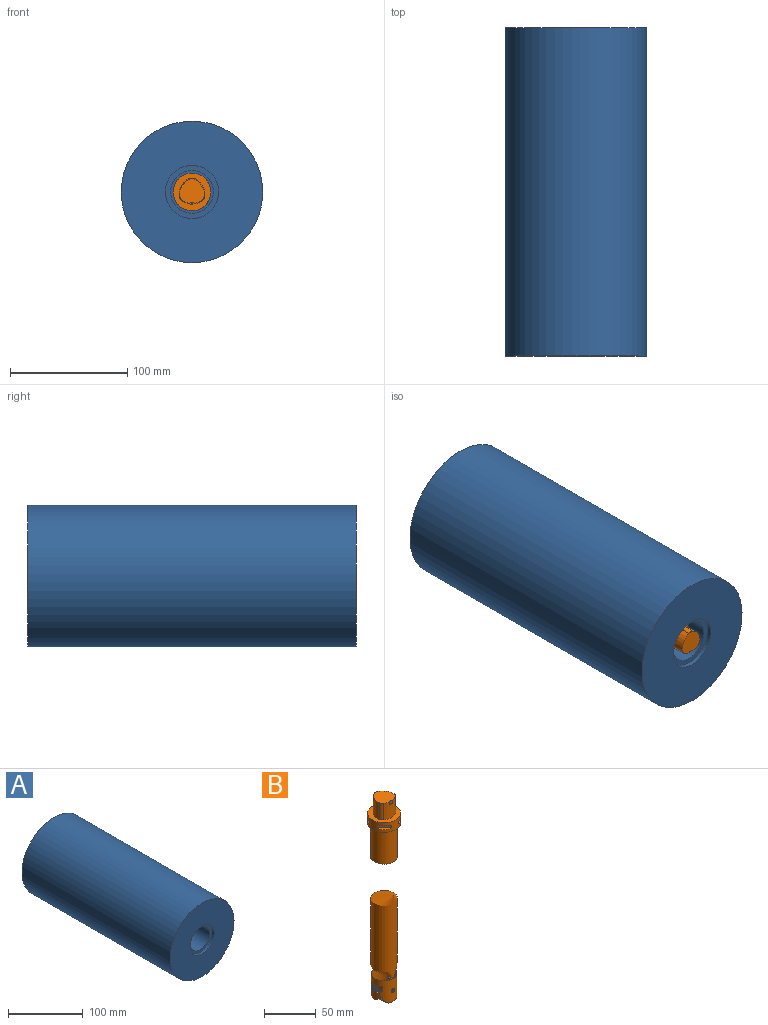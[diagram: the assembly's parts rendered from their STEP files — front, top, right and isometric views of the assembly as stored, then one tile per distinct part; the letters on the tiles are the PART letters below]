
ASSEMBLY  parts=2 mates=1
PART A: 10 faces, bbox 120.5x279.4x120.5 mm
  f0: cylinder r=15.12mm len=200.53mm, axis (0,-1,0), area 19044.7mm2, adj f5,f8
  f1: cylinder r=18.25mm len=36.5mm, axis (0,-1,0), area 3413.5mm2, adj f5,f6
  f2: cylinder r=60.23mm len=279.4mm, axis (0,1,0), area 105740.1mm2, adj f3,f4
  f3: plane 120.47x120.47mm, normal (0,-1,0), area 9788.6mm2, adj f2,f7
  f4: plane 120.47x120.47mm, normal (0,1,0), area 10593.2mm2, adj f2,f9
  f5: plane 36.5x36.5mm, normal (0,-1,0), area 328.6mm2, adj f0,f1
  f6: plane 45.26x45.26mm, normal (0,-1,0), area 562.7mm2, adj f1,f7
  f7: cylinder r=22.63mm len=45.26mm, axis (0,-1,0), area 552.6mm2, adj f3,f6
  f8: plane 32x32mm, normal (0,1,0), area 86.7mm2, adj f0,f9
  f9: cylinder r=16mm len=45.21mm, axis (0,1,0), area 4545.8mm2, adj f4,f8
PART B: 334 faces, bbox 34.1x34.1x237.6 mm
  f0: cylinder r=5mm len=10mm, axis (1,0,0), area 79.2mm2, adj f1,f328,f329,f330,f331,f332,f333
  f1: plane 1.54x0.67mm, normal (0,-1,0), area 0.5mm2, adj f0,f2,f328,f333
  f2: plane 20.16x3.06mm, normal (-0.85,0,-0.53), area 55.5mm2, adj f1,f3,f233,f326,f327,f328,f331,f332
  f3: cone r=11.7mm half-angle=45deg, axis (0,0,1), area 23.6mm2, adj f2,f4,f233,f327
  f4: plane 15.11x12.24mm, normal (1,0,0), area 71.8mm2, adj f3,f5,f7,f9,f10,f11,f13,f14
  f5: plane 1.6x0.58mm, normal (0,0,-1), area 0.1mm2, adj f4,f6,f204,f230
  f6: plane 0.08x0.05mm, normal (-0.34,0.94,0), area 0mm2, adj f5,f204,f229,f230
  f7: plane 0.99x0.36mm, normal (0,-0.13,0.99), area 0mm2, adj f4,f8,f9,f204
  f8: plane 0.08x0.05mm, normal (-0.34,0.93,0.12), area 0mm2, adj f7,f9,f10,f204
  f9: plane 0.86x0.31mm, normal (0.94,0.34,0.04), area 0.1mm2, adj f4,f7,f8,f10
  f10: plane 0.99x0.36mm, normal (0,0.13,-0.99), area 0mm2, adj f4,f8,f9,f204
  f11: plane 0.97x0.36mm, normal (0,-0.25,0.97), area 0mm2, adj f4,f12,f13,f204
  f12: plane 0.08x0.05mm, normal (-0.34,0.91,0.23), area 0mm2, adj f11,f13,f14,f204
  f13: plane 0.85x0.31mm, normal (0.94,0.33,0.09), area 0.1mm2, adj f4,f11,f12,f14
  f14: plane 0.97x0.36mm, normal (0,0.25,-0.97), area 0mm2, adj f4,f12,f13,f204
  f15: plane 0.93x0.37mm, normal (0,-0.37,0.93), area 0mm2, adj f4,f16,f17,f204
  f16: plane 0.08x0.05mm, normal (-0.34,0.87,0.35), area 0mm2, adj f15,f17,f18,f204
  f17: plane 0.82x0.38mm, normal (0.94,0.32,0.13), area 0.1mm2, adj f4,f15,f16,f18
  f18: plane 0.93x0.37mm, normal (0,0.37,-0.93), area 0mm2, adj f4,f16,f17,f204
  f19: plane 0.88x0.48mm, normal (0,-0.48,0.88), area 0mm2, adj f4,f20,f21,f204
  f20: plane 0.07x0.05mm, normal (-0.34,0.82,0.45), area 0mm2, adj f19,f21,f22,f204
  f21: plane 0.78x0.48mm, normal (0.94,0.3,0.16), area 0.1mm2, adj f4,f19,f20,f22
  f22: plane 0.88x0.48mm, normal (0,0.48,-0.88), area 0mm2, adj f4,f20,f21,f204
  f23: plane 1.3x0.94mm, normal (0,-0.59,0.81), area 0.1mm2, adj f4,f24,f25,f204
  f24: plane 0.07x0.06mm, normal (-0.34,0.76,0.55), area 0mm2, adj f23,f25,f26,f204
  f25: plane 1.22x0.92mm, normal (0.94,0.28,0.2), area 0.1mm2, adj f4,f23,f24,f26
  f26: plane 1.3x0.94mm, normal (0,0.59,-0.81), area 0.1mm2, adj f4,f24,f25,f204
  f27: plane 0.73x0.69mm, normal (0,-0.68,0.73), area 0mm2, adj f4,f28,f29,f204
  f28: plane 0.07x0.06mm, normal (-0.34,0.68,0.64), area 0mm2, adj f27,f29,f30,f204
  f29: plane 0.67x0.64mm, normal (0.94,0.25,0.23), area 0.1mm2, adj f4,f27,f28,f30
  f30: plane 0.73x0.69mm, normal (0,0.68,-0.73), area 0mm2, adj f4,f28,f29,f204
  f31: plane 0.77x0.64mm, normal (0,-0.77,0.64), area 0mm2, adj f4,f32,f33,f204
  f32: plane 0.07x0.06mm, normal (-0.34,0.6,0.72), area 0mm2, adj f31,f33,f34,f204
  f33: plane 0.71x0.6mm, normal (0.94,0.22,0.26), area 0.1mm2, adj f4,f31,f32,f34
  f34: plane 0.77x0.64mm, normal (0,0.77,-0.64), area 0mm2, adj f4,f32,f33,f204
  f35: plane 0.84x0.54mm, normal (0,-0.84,0.54), area 0mm2, adj f4,f36,f37,f204
  f36: plane 0.07x0.05mm, normal (-0.34,0.5,0.79), area 0mm2, adj f35,f37,f38,f204
  f37: plane 0.76x0.52mm, normal (0.94,0.18,0.29), area 0.1mm2, adj f4,f35,f36,f38
  f38: plane 0.84x0.54mm, normal (0,0.84,-0.54), area 0mm2, adj f4,f36,f37,f204
  f39: plane 0.91x0.43mm, normal (0,-0.9,0.43), area 0mm2, adj f4,f40,f41,f204
  f40: plane 0.08x0.05mm, normal (-0.34,0.4,0.85), area 0mm2, adj f39,f41,f42,f204
  f41: plane 0.8x0.43mm, normal (0.94,0.15,0.31), area 0.1mm2, adj f4,f39,f40,f42
  f42: plane 0.91x0.43mm, normal (0,0.9,-0.43), area 0mm2, adj f4,f40,f41,f204
  f43: plane 1.52x0.58mm, normal (0,-0.95,0.31), area 0.1mm2, adj f4,f44,f45,f204
  f44: plane 0.08x0.05mm, normal (-0.34,0.29,0.89), area 0mm2, adj f43,f45,f46,f204
  f45: plane 1.41x0.53mm, normal (0.94,0.11,0.33), area 0.1mm2, adj f4,f43,f44,f46
  f46: plane 1.52x0.58mm, normal (0,0.95,-0.31), area 0.1mm2, adj f4,f44,f45,f204
  f47: plane 0.98x0.36mm, normal (0,-0.98,0.19), area 0mm2, adj f4,f48,f49,f204
  f48: plane 0.08x0.05mm, normal (-0.34,0.18,0.92), area 0mm2, adj f47,f49,f50,f204
  f49: plane 0.85x0.31mm, normal (0.94,0.06,0.34), area 0.1mm2, adj f4,f47,f48,f50
  f50: plane 0.98x0.36mm, normal (0,0.98,-0.19), area 0mm2, adj f4,f48,f49,f204
  f51: plane 1x0.36mm, normal (0,-1,0.06), area 0mm2, adj f4,f52,f53,f204
  f52: plane 0.08x0.05mm, normal (-0.34,0.06,0.94), area 0mm2, adj f51,f53,f54,f204
  f53: plane 0.86x0.31mm, normal (0.94,0.02,0.34), area 0.1mm2, adj f4,f51,f52,f54
  f54: plane 1x0.36mm, normal (0,1,-0.06), area 0mm2, adj f4,f52,f53,f204
  f55: plane 1x0.36mm, normal (0,-1,-0.06), area 0mm2, adj f4,f56,f57,f204
  f56: plane 0.08x0.05mm, normal (-0.34,-0.06,0.94), area 0mm2, adj f55,f57,f58,f204
  f57: plane 0.86x0.31mm, normal (0.94,-0.02,0.34), area 0.1mm2, adj f4,f55,f56,f58
  f58: plane 1x0.36mm, normal (0,1,0.06), area 0mm2, adj f4,f56,f57,f204
  f59: plane 0.98x0.36mm, normal (0,-0.98,-0.19), area 0mm2, adj f4,f60,f61,f204
  f60: plane 0.08x0.05mm, normal (-0.34,-0.18,0.92), area 0mm2, adj f59,f61,f62,f204
  f61: plane 0.85x0.31mm, normal (0.94,-0.06,0.34), area 0.1mm2, adj f4,f59,f60,f62
  f62: plane 0.98x0.36mm, normal (0,0.98,0.19), area 0mm2, adj f4,f60,f61,f204
  f63: plane 1.52x0.58mm, normal (0,-0.95,-0.31), area 0.1mm2, adj f4,f64,f65,f204
  f64: plane 0.08x0.05mm, normal (-0.34,-0.29,0.89), area 0mm2, adj f63,f65,f66,f204
  f65: plane 1.41x0.53mm, normal (0.94,-0.11,0.33), area 0.1mm2, adj f4,f63,f64,f66
  f66: plane 1.52x0.58mm, normal (0,0.95,0.31), area 0.1mm2, adj f4,f64,f65,f204
  f67: plane 0.91x0.43mm, normal (0,-0.9,-0.43), area 0mm2, adj f4,f68,f69,f204
  f68: plane 0.08x0.05mm, normal (-0.34,-0.4,0.85), area 0mm2, adj f67,f69,f70,f204
  f69: plane 0.8x0.43mm, normal (0.94,-0.15,0.31), area 0.1mm2, adj f4,f67,f68,f70
  f70: plane 0.91x0.43mm, normal (0,0.9,0.43), area 0mm2, adj f4,f68,f69,f204
  f71: plane 0.84x0.54mm, normal (0,-0.84,-0.54), area 0mm2, adj f4,f72,f73,f204
  f72: plane 0.07x0.05mm, normal (-0.34,-0.5,0.79), area 0mm2, adj f71,f73,f74,f204
  f73: plane 0.76x0.52mm, normal (0.94,-0.18,0.29), area 0.1mm2, adj f4,f71,f72,f74
  f74: plane 0.84x0.54mm, normal (0,0.84,0.54), area 0mm2, adj f4,f72,f73,f204
  f75: plane 0.77x0.64mm, normal (0,-0.77,-0.64), area 0mm2, adj f4,f76,f77,f204
  f76: plane 0.07x0.06mm, normal (-0.34,-0.6,0.72), area 0mm2, adj f75,f77,f78,f204
  f77: plane 0.71x0.6mm, normal (0.94,-0.22,0.26), area 0.1mm2, adj f4,f75,f76,f78
  f78: plane 0.77x0.64mm, normal (0,0.77,0.64), area 0mm2, adj f4,f76,f77,f204
  f79: plane 0.73x0.69mm, normal (0,-0.68,-0.73), area 0mm2, adj f4,f80,f81,f204
  f80: plane 0.07x0.06mm, normal (-0.34,-0.68,0.64), area 0mm2, adj f79,f81,f82,f204
  f81: plane 0.67x0.64mm, normal (0.94,-0.25,0.23), area 0.1mm2, adj f4,f79,f80,f82
  f82: plane 0.73x0.69mm, normal (0,0.68,0.73), area 0mm2, adj f4,f80,f81,f204
  f83: plane 1.3x0.94mm, normal (0,-0.59,-0.81), area 0.1mm2, adj f4,f84,f85,f204
  f84: plane 0.07x0.06mm, normal (-0.34,-0.76,0.55), area 0mm2, adj f83,f85,f86,f204
  f85: plane 1.22x0.92mm, normal (0.94,-0.28,0.2), area 0.1mm2, adj f4,f83,f84,f86
  f86: plane 1.3x0.94mm, normal (0,0.59,0.81), area 0.1mm2, adj f4,f84,f85,f204
  f87: plane 0.88x0.48mm, normal (0,-0.48,-0.88), area 0mm2, adj f4,f88,f89,f204
  f88: plane 0.07x0.05mm, normal (-0.34,-0.82,0.45), area 0mm2, adj f87,f89,f90,f204
  f89: plane 0.78x0.48mm, normal (0.94,-0.3,0.16), area 0.1mm2, adj f4,f87,f88,f90
  f90: plane 0.88x0.48mm, normal (0,0.48,0.88), area 0mm2, adj f4,f88,f89,f204
  f91: plane 0.93x0.37mm, normal (0,-0.37,-0.93), area 0mm2, adj f4,f92,f93,f204
  f92: plane 0.08x0.05mm, normal (-0.34,-0.87,0.35), area 0mm2, adj f91,f93,f94,f204
  f93: plane 0.82x0.38mm, normal (0.94,-0.32,0.13), area 0.1mm2, adj f4,f91,f92,f94
  f94: plane 0.93x0.37mm, normal (0,0.37,0.93), area 0mm2, adj f4,f92,f93,f204
  f95: plane 0.97x0.36mm, normal (0,-0.25,-0.97), area 0mm2, adj f4,f96,f97,f204
  f96: plane 0.08x0.05mm, normal (-0.34,-0.91,0.23), area 0mm2, adj f95,f97,f98,f204
  f97: plane 0.85x0.31mm, normal (0.94,-0.33,0.09), area 0.1mm2, adj f4,f95,f96,f98
  f98: plane 0.97x0.36mm, normal (0,0.25,0.97), area 0mm2, adj f4,f96,f97,f204
  f99: plane 0.99x0.36mm, normal (0,-0.13,-0.99), area 0mm2, adj f4,f100,f101,f204
  f100: plane 0.08x0.05mm, normal (-0.34,-0.93,0.12), area 0mm2, adj f99,f101,f102,f204
  f101: plane 0.86x0.31mm, normal (0.94,-0.34,0.04), area 0.1mm2, adj f4,f99,f100,f102
  f102: plane 0.99x0.36mm, normal (0,0.13,0.99), area 0mm2, adj f4,f100,f101,f204
  f103: plane 1.6x0.58mm, normal (0,0,-1), area 0.1mm2, adj f4,f104,f105,f204
  f104: plane 0.08x0.05mm, normal (-0.34,-0.94,0), area 0mm2, adj f103,f105,f106,f204
  f105: plane 1.45x0.53mm, normal (0.94,-0.34,0), area 0.1mm2, adj f4,f103,f104,f106
  f106: plane 1.6x0.58mm, normal (0,0,1), area 0.1mm2, adj f4,f104,f105,f204
  f107: plane 0.99x0.36mm, normal (0,0.13,-0.99), area 0mm2, adj f4,f108,f109,f204
  f108: plane 0.08x0.05mm, normal (-0.34,-0.93,-0.12), area 0mm2, adj f107,f109,f110,f204
  f109: plane 0.86x0.31mm, normal (0.94,-0.34,-0.04), area 0.1mm2, adj f4,f107,f108,f110
  f110: plane 0.99x0.36mm, normal (0,-0.13,0.99), area 0mm2, adj f4,f108,f109,f204
  f111: plane 0.97x0.36mm, normal (0,0.25,-0.97), area 0mm2, adj f4,f112,f113,f204
  f112: plane 0.08x0.05mm, normal (-0.34,-0.91,-0.23), area 0mm2, adj f111,f113,f114,f204
  f113: plane 0.85x0.31mm, normal (0.94,-0.33,-0.09), area 0.1mm2, adj f4,f111,f112,f114
  f114: plane 0.97x0.36mm, normal (0,-0.25,0.97), area 0mm2, adj f4,f112,f113,f204
  f115: plane 0.93x0.37mm, normal (0,0.37,-0.93), area 0mm2, adj f4,f116,f117,f204
  f116: plane 0.08x0.05mm, normal (-0.34,-0.87,-0.35), area 0mm2, adj f115,f117,f118,f204
  f117: plane 0.82x0.38mm, normal (0.94,-0.32,-0.13), area 0.1mm2, adj f4,f115,f116,f118
  f118: plane 0.93x0.37mm, normal (0,-0.37,0.93), area 0mm2, adj f4,f116,f117,f204
  f119: plane 0.88x0.48mm, normal (0,0.48,-0.88), area 0mm2, adj f4,f120,f121,f204
  f120: plane 0.07x0.05mm, normal (-0.34,-0.82,-0.45), area 0mm2, adj f119,f121,f122,f204
  f121: plane 0.78x0.48mm, normal (0.94,-0.3,-0.16), area 0.1mm2, adj f4,f119,f120,f122
  f122: plane 0.88x0.48mm, normal (0,-0.48,0.88), area 0mm2, adj f4,f120,f121,f204
  f123: plane 1.3x0.94mm, normal (0,0.59,-0.81), area 0.1mm2, adj f4,f124,f125,f204
  f124: plane 0.07x0.06mm, normal (-0.34,-0.76,-0.55), area 0mm2, adj f123,f125,f126,f204
  f125: plane 1.22x0.92mm, normal (0.94,-0.28,-0.2), area 0.1mm2, adj f4,f123,f124,f126
  f126: plane 1.3x0.94mm, normal (0,-0.59,0.81), area 0.1mm2, adj f4,f124,f125,f204
  f127: plane 0.73x0.69mm, normal (0,0.68,-0.73), area 0mm2, adj f4,f128,f129,f204
  f128: plane 0.07x0.06mm, normal (-0.34,-0.68,-0.64), area 0mm2, adj f127,f129,f130,f204
  f129: plane 0.67x0.64mm, normal (0.94,-0.25,-0.23), area 0.1mm2, adj f4,f127,f128,f130
  f130: plane 0.73x0.69mm, normal (0,-0.68,0.73), area 0mm2, adj f4,f128,f129,f204
  f131: plane 0.77x0.64mm, normal (0,0.77,-0.64), area 0mm2, adj f4,f132,f133,f204
  f132: plane 0.07x0.06mm, normal (-0.34,-0.6,-0.72), area 0mm2, adj f131,f133,f134,f204
  f133: plane 0.71x0.6mm, normal (0.94,-0.22,-0.26), area 0.1mm2, adj f4,f131,f132,f134
  f134: plane 0.77x0.64mm, normal (0,-0.77,0.64), area 0mm2, adj f4,f132,f133,f204
  f135: plane 0.84x0.54mm, normal (0,0.84,-0.54), area 0mm2, adj f4,f136,f137,f204
  f136: plane 0.07x0.05mm, normal (-0.34,-0.5,-0.79), area 0mm2, adj f135,f137,f138,f204
  f137: plane 0.76x0.52mm, normal (0.94,-0.18,-0.29), area 0.1mm2, adj f4,f135,f136,f138
  f138: plane 0.84x0.54mm, normal (0,-0.84,0.54), area 0mm2, adj f4,f136,f137,f204
  f139: plane 0.91x0.43mm, normal (0,0.9,-0.43), area 0mm2, adj f4,f140,f141,f204
  f140: plane 0.08x0.05mm, normal (-0.34,-0.4,-0.85), area 0mm2, adj f139,f141,f142,f204
  f141: plane 0.8x0.43mm, normal (0.94,-0.15,-0.31), area 0.1mm2, adj f4,f139,f140,f142
  f142: plane 0.91x0.43mm, normal (0,-0.9,0.43), area 0mm2, adj f4,f140,f141,f204
  f143: plane 1.52x0.58mm, normal (0,0.95,-0.31), area 0.1mm2, adj f4,f144,f145,f204
  f144: plane 0.08x0.05mm, normal (-0.34,-0.29,-0.89), area 0mm2, adj f143,f145,f146,f204
  f145: plane 1.41x0.53mm, normal (0.94,-0.11,-0.33), area 0.1mm2, adj f4,f143,f144,f146
  f146: plane 1.52x0.58mm, normal (0,-0.95,0.31), area 0.1mm2, adj f4,f144,f145,f204
  f147: plane 0.98x0.36mm, normal (0,0.98,-0.19), area 0mm2, adj f4,f148,f149,f204
  f148: plane 0.08x0.05mm, normal (-0.34,-0.18,-0.92), area 0mm2, adj f147,f149,f150,f204
  f149: plane 0.85x0.31mm, normal (0.94,-0.06,-0.34), area 0.1mm2, adj f4,f147,f148,f150
  f150: plane 0.98x0.36mm, normal (0,-0.98,0.19), area 0mm2, adj f4,f148,f149,f204
  f151: plane 1x0.36mm, normal (0,1,-0.06), area 0mm2, adj f4,f152,f153,f204
  f152: plane 0.08x0.05mm, normal (-0.34,-0.06,-0.94), area 0mm2, adj f151,f153,f154,f204
  f153: plane 0.86x0.31mm, normal (0.94,-0.02,-0.34), area 0.1mm2, adj f4,f151,f152,f154
  f154: plane 1x0.36mm, normal (0,-1,0.06), area 0mm2, adj f4,f152,f153,f204
  f155: cone r=2.25mm half-angle=70deg, axis (-1,0,0), area 0mm2, adj f4,f156,f204
  f156: plane 1x0.36mm, normal (0,1,0.06), area 0mm2, adj f4,f155,f157,f158
  f157: plane 0.08x0.05mm, normal (-0.34,0.06,-0.94), area 0mm2, adj f156,f158,f159,f204
  f158: plane 0.86x0.31mm, normal (0.94,0.02,-0.34), area 0.1mm2, adj f4,f156,f157,f159
  f159: plane 1x0.36mm, normal (0,-1,-0.06), area 0mm2, adj f4,f157,f158,f204
  f160: plane 0.98x0.36mm, normal (0,0.98,0.19), area 0mm2, adj f4,f161,f162,f204
  f161: plane 0.08x0.05mm, normal (-0.34,0.18,-0.92), area 0mm2, adj f160,f162,f163,f204
  f162: plane 0.85x0.31mm, normal (0.94,0.06,-0.34), area 0.1mm2, adj f4,f160,f161,f163
  f163: plane 0.98x0.36mm, normal (0,-0.98,-0.19), area 0mm2, adj f4,f161,f162,f204
  f164: plane 1.52x0.58mm, normal (0,0.95,0.31), area 0.1mm2, adj f4,f165,f166,f204
  f165: plane 0.08x0.05mm, normal (-0.34,0.29,-0.89), area 0mm2, adj f164,f166,f167,f204
  f166: plane 1.41x0.53mm, normal (0.94,0.11,-0.33), area 0.1mm2, adj f4,f164,f165,f167
  f167: plane 1.52x0.58mm, normal (0,-0.95,-0.31), area 0.1mm2, adj f4,f165,f166,f204
  f168: plane 0.91x0.43mm, normal (0,0.9,0.43), area 0mm2, adj f4,f169,f170,f204
  f169: plane 0.08x0.05mm, normal (-0.34,0.4,-0.85), area 0mm2, adj f168,f170,f171,f204
  f170: plane 0.8x0.43mm, normal (0.94,0.15,-0.31), area 0.1mm2, adj f4,f168,f169,f171
  f171: plane 0.91x0.43mm, normal (0,-0.9,-0.43), area 0mm2, adj f4,f169,f170,f204
  f172: plane 0.84x0.54mm, normal (0,0.84,0.54), area 0mm2, adj f4,f173,f174,f204
  f173: plane 0.07x0.05mm, normal (-0.34,0.5,-0.79), area 0mm2, adj f172,f174,f175,f204
  f174: plane 0.76x0.52mm, normal (0.94,0.18,-0.29), area 0.1mm2, adj f4,f172,f173,f175
  f175: plane 0.84x0.54mm, normal (0,-0.84,-0.54), area 0mm2, adj f4,f173,f174,f204
  f176: plane 0.77x0.64mm, normal (0,0.77,0.64), area 0mm2, adj f4,f177,f178,f204
  f177: plane 0.07x0.06mm, normal (-0.34,0.6,-0.72), area 0mm2, adj f176,f178,f179,f204
  f178: plane 0.71x0.6mm, normal (0.94,0.22,-0.26), area 0.1mm2, adj f4,f176,f177,f179
  f179: plane 0.77x0.64mm, normal (0,-0.77,-0.64), area 0mm2, adj f4,f177,f178,f204
  f180: plane 0.73x0.69mm, normal (0,0.68,0.73), area 0mm2, adj f4,f181,f182,f204
  f181: plane 0.07x0.06mm, normal (-0.34,0.68,-0.64), area 0mm2, adj f180,f182,f183,f204
  f182: plane 0.67x0.64mm, normal (0.94,0.25,-0.23), area 0.1mm2, adj f4,f180,f181,f183
  f183: plane 0.73x0.69mm, normal (0,-0.68,-0.73), area 0mm2, adj f4,f181,f182,f204
  f184: plane 1.3x0.94mm, normal (0,0.59,0.81), area 0.1mm2, adj f4,f185,f186,f204
  f185: plane 0.07x0.06mm, normal (-0.34,0.76,-0.55), area 0mm2, adj f184,f186,f187,f204
  f186: plane 1.22x0.92mm, normal (0.94,0.28,-0.2), area 0.1mm2, adj f4,f184,f185,f187
  f187: plane 1.3x0.94mm, normal (0,-0.59,-0.81), area 0.1mm2, adj f4,f185,f186,f204
  f188: plane 0.88x0.48mm, normal (0,0.48,0.88), area 0mm2, adj f4,f189,f190,f204
  f189: plane 0.07x0.05mm, normal (-0.34,0.82,-0.45), area 0mm2, adj f188,f190,f191,f204
  f190: plane 0.78x0.48mm, normal (0.94,0.3,-0.16), area 0.1mm2, adj f4,f188,f189,f191
  f191: plane 0.88x0.48mm, normal (0,-0.48,-0.88), area 0mm2, adj f4,f189,f190,f204
  f192: plane 0.93x0.37mm, normal (0,0.37,0.93), area 0mm2, adj f4,f193,f194,f204
  f193: plane 0.08x0.05mm, normal (-0.34,0.87,-0.35), area 0mm2, adj f192,f194,f195,f204
  f194: plane 0.82x0.38mm, normal (0.94,0.32,-0.13), area 0.1mm2, adj f4,f192,f193,f195
  f195: plane 0.93x0.37mm, normal (0,-0.37,-0.93), area 0mm2, adj f4,f193,f194,f204
  f196: plane 0.97x0.36mm, normal (0,0.25,0.97), area 0mm2, adj f4,f197,f198,f204
  f197: plane 0.08x0.05mm, normal (-0.34,0.91,-0.23), area 0mm2, adj f196,f198,f199,f204
  f198: plane 0.85x0.31mm, normal (0.94,0.33,-0.09), area 0.1mm2, adj f4,f196,f197,f199
  f199: plane 0.97x0.36mm, normal (0,-0.25,-0.97), area 0mm2, adj f4,f197,f198,f204
  f200: plane 0.99x0.36mm, normal (0,0.13,0.99), area 0mm2, adj f4,f201,f202,f204
  f201: plane 0.08x0.05mm, normal (-0.34,0.93,-0.12), area 0mm2, adj f200,f202,f203,f204
  f202: plane 0.86x0.31mm, normal (0.94,0.34,-0.04), area 0.1mm2, adj f4,f200,f201,f203
  f203: plane 0.99x0.36mm, normal (0,-0.13,-0.99), area 0mm2, adj f4,f201,f202,f204
  f204: cone r=2.25mm half-angle=70deg, axis (-1,0,0), area 94.8mm2, adj f4,f5,f6,f7,f8,f10,f11,f12
  f205: plane 4.51x4.51mm, normal (1,0,0), area 8mm2, adj f204,f206
  f206: cone r=1.59mm half-angle=30deg, axis (1,0,0), area 1.7mm2, adj f205,f207
  f207: cylinder r=1.5mm len=3mm, axis (-1,0,0), area 3.3mm2, adj f206,f208
  f208: cone r=1.5mm half-angle=45deg, axis (1,0,0), area 1.9mm2, adj f207,f209,f211,f213,f214,f216,f217,f219
  f209: plane 2.21x0.43mm, normal (0,-0.5,-0.87), area 0.9mm2, adj f208,f210,f226,f228
  f210: plane 0.76x0.22mm, normal (1,0,0), area 0.1mm2, adj f209,f226,f228
  f211: plane 2.21x0.43mm, normal (0,-0.5,-0.87), area 0.9mm2, adj f208,f212,f213,f226
  f212: plane 0.66x0.38mm, normal (1,0,0), area 0.1mm2, adj f211,f213,f226
  f213: plane 2.21x0.49mm, normal (0,-1,0), area 0.9mm2, adj f208,f211,f212,f226
  f214: plane 2.21x0.49mm, normal (0,-1,0), area 0.9mm2, adj f208,f215,f216,f226
  f215: plane 0.66x0.38mm, normal (1,0,0), area 0.1mm2, adj f214,f216,f226
  f216: plane 2.21x0.43mm, normal (0,-0.5,0.87), area 0.9mm2, adj f208,f214,f215,f226
  f217: plane 2.21x0.43mm, normal (0,-0.5,0.87), area 0.9mm2, adj f208,f218,f219,f226
  f218: plane 0.76x0.22mm, normal (1,0,0), area 0.1mm2, adj f217,f219,f226
  f219: plane 2.21x0.43mm, normal (0,0.5,0.87), area 0.9mm2, adj f208,f217,f218,f226
  f220: plane 2.21x0.43mm, normal (0,0.5,0.87), area 0.9mm2, adj f208,f221,f222,f226
  f221: plane 0.66x0.38mm, normal (1,0,0), area 0.1mm2, adj f220,f222,f226
  f222: plane 2.21x0.49mm, normal (0,1,0), area 0.9mm2, adj f208,f220,f221,f226
  f223: plane 2.21x0.49mm, normal (0,1,0), area 0.9mm2, adj f208,f224,f225,f226
  f224: plane 0.66x0.38mm, normal (1,0,0), area 0.1mm2, adj f223,f225,f226
  f225: plane 2.21x0.43mm, normal (0,0.5,-0.87), area 0.9mm2, adj f208,f223,f224,f226
  f226: cylinder r=1.3mm len=2.6mm, axis (1,0,0), area 12mm2, adj f208,f209,f210,f211,f212,f213,f214,f215
  f227: cone r=1.3mm half-angle=70deg, axis (1,0,0), area 5.7mm2, adj f226
  f228: plane 2.21x0.43mm, normal (0,0.5,-0.87), area 0.9mm2, adj f208,f209,f210,f226
  f229: plane 1.6x0.58mm, normal (0,0,1), area 0.1mm2, adj f4,f6,f204,f230
  f230: plane 1.45x0.53mm, normal (0.94,0.34,0), area 0.1mm2, adj f4,f5,f6,f229
  f231: cone r=11.7mm half-angle=45deg, axis (0,0,1), area 20.6mm2, adj f4,f233,f326,f327
  f232: plane 12.12x1.57mm, normal (0.71,0,-0.71), area 18.1mm2, adj f4,f233
  f233: cylinder r=12.5mm len=26.7mm, axis (0,0,-1), area 1534.3mm2, adj f2,f3,f4,f231,f232,f234,f244,f248
  f234: cylinder r=2.12mm len=4.25mm, axis (0,1,0), area 10.3mm2, adj f233,f235
  f235: plane 4.25x4.25mm, normal (0,-1,0), area 1.6mm2, adj f234,f236
  f236: cylinder r=2mm len=4mm, axis (0,1,0), area 8.2mm2, adj f235,f237
  f237: cone r=2mm half-angle=45deg, axis (0,1,0), area 0.9mm2, adj f236,f238
  f238: plane 3.9x3.9mm, normal (0,-1,0), area 4.9mm2, adj f237,f239
  f239: cone r=1.5mm half-angle=60deg, axis (0,-1,0), area 7.3mm2, adj f238,f240
  f240: cylinder r=0.5mm len=1mm, axis (0,1,0), area 0.3mm2, adj f239,f241
  f241: cone r=0.75mm half-angle=60deg, axis (0,1,0), area 0.1mm2, adj f240,f242
  f242: plane 1.08x1.08mm, normal (0,-1,0), area 0.2mm2, adj f241,f243
  f243: sphere r=0.65mm, area 0.9mm2, adj f242
  f244: cylinder r=2.01mm len=4.02mm, axis (0,-1,0), area 9.7mm2, adj f233,f245
  f245: plane 4.02x4.02mm, normal (0,1,0), area 0.1mm2, adj f244,f246
  f246: cylinder r=2mm len=4mm, axis (0,-1,0), area 4.5mm2, adj f245,f247
  f247: sphere r=5.8mm, area 12.8mm2, adj f246
  f248: cylinder r=2.6mm len=5.19mm, axis (0,-1,0), area 7.2mm2, adj f233,f249
  f249: plane 5.19x5.19mm, normal (0,1,0), area 1.5mm2, adj f248,f250
  f250: cylinder r=2.5mm len=5mm, axis (0,-1,0), area 2.3mm2, adj f249,f251
  f251: cone r=2mm half-angle=45deg, axis (0,-1,0), area 10mm2, adj f250,f252
  f252: plane 4x4mm, normal (0,1,0), area 7.2mm2, adj f251,f253,f262,f263,f264,f265,f266
  f253: plane 3.2x1.22mm, normal (-0.85,0,0.53), area 4.6mm2, adj f252,f254,f261,f262,f266
  f254: plane 1.25x0.38mm, normal (0,1,0), area 0.1mm2, adj f253,f255,f266
  f255: cylinder r=1.25mm len=2.5mm, axis (0,-1,0), area 3.9mm2, adj f254,f256,f257,f258,f259,f260,f261
  f256: plane 1.06x0.67mm, normal (0,1,0), area 0.1mm2, adj f255,f262,f263
  f257: plane 1.25x0.38mm, normal (0,1,0), area 0.1mm2, adj f255,f263,f264
  f258: plane 1.11x0.61mm, normal (0,1,0), area 0.1mm2, adj f255,f264,f265
  f259: plane 1.06x0.67mm, normal (0,1,0), area 0.1mm2, adj f255,f265,f266
  f260: cone r=1.25mm half-angle=70deg, axis (0,1,0), area 5.2mm2, adj f255
  f261: plane 1.11x0.61mm, normal (0,1,0), area 0.1mm2, adj f253,f255,f262
  f262: plane 3.2x1.44mm, normal (0.04,0,1), area 4.6mm2, adj f252,f253,f256,f261,f263
  f263: plane 3.2x1.28mm, normal (0.88,0,0.47), area 4.6mm2, adj f252,f256,f257,f262,f264
  f264: plane 3.2x1.22mm, normal (0.85,0,-0.53), area 4.6mm2, adj f252,f257,f258,f263,f265
  f265: plane 3.2x1.44mm, normal (-0.04,0,-1), area 4.6mm2, adj f252,f258,f259,f264,f266
  f266: plane 3.2x1.28mm, normal (-0.88,0,-0.47), area 4.6mm2, adj f252,f253,f254,f259,f265
  f267: plane 6.1x2.35mm, normal (0,0,1), area 1mm2, adj f233,f268,f299
  f268: torus R=32.4mm, axis (0,0,-1), area 3.6mm2, adj f233,f267,f271,f299
  f269: plane 13.8x2.23mm, normal (0,0,-1), area 12.6mm2, adj f233,f270
  f270: torus R=32.4mm, axis (0,0,1), area 9.3mm2, adj f233,f269,f271
  f271: cylinder r=32mm len=15.48mm, axis (0,0,1), area 51.3mm2, adj f233,f268,f270,f272,f294,f295,f296,f297
  f272: plane 3x1.2mm, normal (0,0,-1), area 3.5mm2, adj f271,f273,f294,f296
  f273: cylinder r=0.4mm len=3mm, axis (0,-1,0), area 1.9mm2, adj f272,f274,f276,f293
  f274: torus R=2.1mm, axis (1,0,0), area 4.6mm2, adj f273,f275,f276,f294
  f275: cylinder r=0.4mm len=3mm, axis (0,-1,0), area 1.9mm2, adj f274,f276,f293,f295
  f276: plane 7.4x4.4mm, normal (-1,0,0), area 23.3mm2, adj f273,f274,f275,f277,f293
  f277: cylinder r=1mm len=2.04mm, axis (1,0.08,0), area 3mm2, adj f276,f278
  f278: cone r=1mm half-angle=30deg, axis (1,0.08,0), area 2.7mm2, adj f277,f279
  f279: plane 1.51x1.5mm, normal (-1,-0.08,0), area 1.1mm2, adj f278,f280,f288,f289,f290,f291,f292
  f280: plane 0.83x0.48mm, normal (0.05,-0.6,-0.8), area 0.4mm2, adj f279,f281,f287,f288,f292
  f281: plane 0.45x0.16mm, normal (-1,-0.08,0), area 0mm2, adj f280,f282,f292
  f282: cone r=1.73mm half-angle=60deg, axis (-1,-0.08,0), area 0.7mm2, adj f281,f283,f284,f285,f286,f287
  f283: plane 0.36x0.27mm, normal (-1,-0.08,0), area 0mm2, adj f282,f288,f289
  f284: plane 0.45x0.16mm, normal (-1,-0.08,0), area 0mm2, adj f282,f289,f290
  f285: plane 0.42x0.21mm, normal (-1,-0.08,0), area 0mm2, adj f282,f290,f291
  f286: plane 0.36x0.27mm, normal (-1,-0.08,0), area 0mm2, adj f282,f291,f292
  f287: plane 0.42x0.21mm, normal (-1,-0.08,0), area 0mm2, adj f280,f282,f288
  f288: plane 0.8x0.52mm, normal (0.08,-0.99,0.13), area 0.4mm2, adj f279,f280,f283,f287,f289
  f289: plane 0.84x0.54mm, normal (0.03,-0.38,0.92), area 0.4mm2, adj f279,f283,f284,f288,f290
  f290: plane 0.83x0.48mm, normal (-0.05,0.6,0.8), area 0.4mm2, adj f279,f284,f285,f289,f291
  f291: plane 0.8x0.52mm, normal (-0.08,0.99,-0.13), area 0.4mm2, adj f279,f285,f286,f290,f292
  f292: plane 0.84x0.54mm, normal (-0.03,0.38,-0.92), area 0.4mm2, adj f279,f280,f281,f286,f291
  f293: torus R=2.1mm, axis (1,0,0), area 4.6mm2, adj f273,f275,f276,f296
  f294: cylinder r=2.5mm len=5mm, axis (-1,0,0), area 9mm2, adj f271,f272,f274,f295
  f295: plane 3x1.2mm, normal (0,0,1), area 3.5mm2, adj f271,f275,f294,f296
  f296: cylinder r=2.5mm len=5mm, axis (-1,0,0), area 9.2mm2, adj f271,f272,f293,f295
  f297: torus R=32.4mm, axis (0,0,-1), area 2.8mm2, adj f233,f271,f298,f299
  f298: plane 3.16x0.46mm, normal (0,0,1), area 0.5mm2, adj f233,f297,f299
  f299: plane 13.37x2.04mm, normal (-0.85,0,0.53), area 5.4mm2, adj f233,f267,f268,f297,f298,f330
  f300: cone r=13mm half-angle=0.2deg, axis (0,0,1), area 11055.3mm2, adj f233,f301
  f301: cylinder r=13mm len=39.5mm, axis (0,0,-1), area 3226.4mm2, adj f300,f302
  f302: plane 32x32mm, normal (0,0,-1), area 273.3mm2, adj f301,f303
  f303: cylinder r=16mm len=32mm, axis (0,0,-1), area 1001.3mm2, adj f302,f304,f305,f306,f307,f308,f309,f310
  f304: plane 12.64x12.64mm, normal (0.35,0.35,0.87), area 21.3mm2, adj f303,f306
  f305: plane 12.64x12.64mm, normal (0.35,0.35,-0.87), area 21.3mm2, adj f303,f306
  f306: plane 10.52x10.52mm, normal (0.71,0.71,0), area 37.2mm2, adj f303,f304,f305
  f307: plane 12.64x12.64mm, normal (-0.35,-0.35,0.87), area 21.3mm2, adj f303,f309
  f308: plane 12.64x12.64mm, normal (-0.35,-0.35,-0.87), area 21.3mm2, adj f303,f309
  f309: plane 10.52x10.52mm, normal (-0.71,-0.71,0), area 37.2mm2, adj f303,f307,f308
  f310: plane 12.64x12.64mm, normal (-0.35,0.35,0.87), area 21.3mm2, adj f303,f312
  f311: plane 12.64x12.64mm, normal (-0.35,0.35,-0.87), area 21.3mm2, adj f303,f312
  f312: plane 10.52x10.52mm, normal (-0.71,0.71,0), area 37.2mm2, adj f303,f310,f311
  f313: plane 12.64x12.64mm, normal (0.35,-0.35,0.87), area 21.3mm2, adj f303,f315
  f314: plane 12.64x12.64mm, normal (0.35,-0.35,-0.87), area 21.3mm2, adj f303,f315
  f315: plane 10.52x10.52mm, normal (0.71,-0.71,0), area 37.2mm2, adj f303,f313,f314
  f316: plane 32x32mm, normal (0,0,1), area 431.2mm2, adj f303,f317,f321,f322,f323,f324,f325
  f317: cone r=15mm half-angle=1.4deg, axis (0,0,-1), area 309.5mm2, adj f316,f318,f319,f320,f321,f325
  f318: plane 20.93x20.91mm, normal (0,0,1), area 338.2mm2, adj f317,f320,f321,f322,f323,f324,f325
  f319: plane 4.68x0.94mm, normal (0,0,1), area 3mm2, adj f317,f320
  f320: cylinder r=4mm len=4.68mm, axis (0,0,-1), area 16.3mm2, adj f317,f318,f319
  f321: cone r=6mm half-angle=1.4deg, axis (0,0,-1), area 102.5mm2, adj f316,f317,f318,f322
  f322: cone r=15mm half-angle=1.4deg, axis (0,0,-1), area 327.4mm2, adj f316,f318,f321,f323
  f323: cone r=6mm half-angle=1.4deg, axis (0,0,-1), area 102.5mm2, adj f316,f318,f322,f324
  f324: cone r=15mm half-angle=1.4deg, axis (0,0,-1), area 324.9mm2, adj f316,f318,f323,f325
  f325: cone r=6mm half-angle=1.4deg, axis (0,0,-1), area 101.7mm2, adj f316,f317,f318,f324
  f326: plane 11.52x4.21mm, normal (-0.48,-0.12,-0.87), area 26.3mm2, adj f2,f231,f233,f327
  f327: plane 23.4x17.44mm, normal (0,0,-1), area 340.9mm2, adj f2,f3,f4,f231,f326
  f328: plane 7.35x6.76mm, normal (-0.93,0,-0.38), area 26.1mm2, adj f0,f1,f2,f233,f330
  f329: cylinder r=13mm len=10mm, axis (0,0,-1), area 80.1mm2, adj f0
  f330: plane 10.79x4.04mm, normal (-1,0,0), area 19.7mm2, adj f0,f233,f299,f328,f331
  f331: plane 7.07x4.53mm, normal (-0.93,0,-0.38), area 19.9mm2, adj f0,f2,f233,f330,f332
  f332: plane 5.68x2.36mm, normal (0,1,0), area 6.8mm2, adj f0,f2,f331,f333
  f333: plane 7.8x5.68mm, normal (-1,0,0), area 11.4mm2, adj f0,f1,f2,f332
PLACE A t=(6.91,100.31,-56.62)mm
PLACE B rot(axis=(1,0,0),90deg) t=(5.73,-158.86,-56.62)mm
MATE cylindrical B.f300 <-> A.f1  axis (0,-1,0) through (6.91,30.14,-56.62)mm
